# Revit family: CC 800
name_source: partatom
category: Mechanical Equipment
units: mm (PartAtom-declared; Revit-internal decimal feet)

## family parameters
Always vertical = Yes
Cut with Voids When Loaded = No
OmniClass Number = 23.75.00.00
OmniClass Title = Climate Control (HVAC)
Part Type = Normal
Room Calculation Point = No
Round Connector Dimension = Use Diameter
Shared = No
Work Plane-Based = No

## types (1)
- CC 800
    Condensate = 9 mm  [stored 0.0295276 ft]
    Electrical connection = 1 ~ 230 V / N / PE / 50 Hz
    Exhaust Air = 315 mm
    L-C Duct Exhaust = 255 mm  [stored 0.836614 ft]
    Manufacturer = Airmaster A/S
    Max. flow rate 30 dB(A) with ePM10 50% filters = 430 m³
    Max. flow rate 30 dB(A) with ePM10 55% filters = 387 m³
    Max. flow rate 30 dB(A) with ePM10 80% filters = 344 m³
    Max. flow rate 35 dB(A) with ePM10 50% filters = 550 m³
    Max. flow rate 35 dB(A) with ePM10 55% filters = 495 m³
    Max. flow rate 35 dB(A) with ePM10 80% filters = 440 m³
    Model = CC 800
    Nominal current,Cooling = 6,8 A
    Phase 1 - Max Current = 6,8 A
    Phase 1 - Max Power Consumption = 1110 W
    R-C Duct Supply = 222 mm
    Suply Air In = 315 mm
    T-C Duct Exhaust = 250 mm  [stored 0.82021 ft]
    T-C Duct Supply = 250 mm  [stored 0.82021 ft]
    Total Depth = 1184 mm  [stored 3.88451 ft]
    Total Hight = 474 mm  [stored 1.55512 ft]
    Total Width = 1910 mm  [stored 6.2664 ft]
    URL = www.airmaster-as.com
    Water Heater Surface IN = 10 mm  [stored 0.0328084 ft]
    Water Heater Surface Return = 10 mm  [stored 0.0328084 ft]
    Weight (Standard Unit) = 100.7

note: [stored X ft] marks values corroborated as IEEE doubles in the binary element streams (Revit-internal decimal feet)

## geometry (parser evidence)
native form markers: Sweep x5
no freeform markers — native parametric forms only
